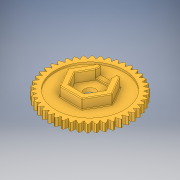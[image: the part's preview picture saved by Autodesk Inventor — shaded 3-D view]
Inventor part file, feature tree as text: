
AUTODESK INVENTOR PART (.ipt)
format: ipt  version: 2019.1 (Build 231200000, 200)  size: 438,272 bytes
history: mixed  units: in
note: dims shown in document units (in); Inventor stores cm internally (conversion verified against a paired STEP export)
features: fillet x1, imported_body x1
ambient origin geometry x8: Origin, YZ Plane, XZ Plane, XY Plane, X Axis, Y Axis, Z Axis, Center Point
bodies: Solid1 (imported_parasolid)
feature tree (2):
  fillet  "Fillet3"  [1 undecoded]
  imported_body  NMx_Import_Brep_tag  [imported B-rep: ~11 faces, bbox_mm=[4.056079, 0.3, 12.5]]
note: 1 required parameter value undecoded (feature->parameter linkage not recoverable at this tier; creation-order binding heuristic only, values carry confidence <= 0.55)
